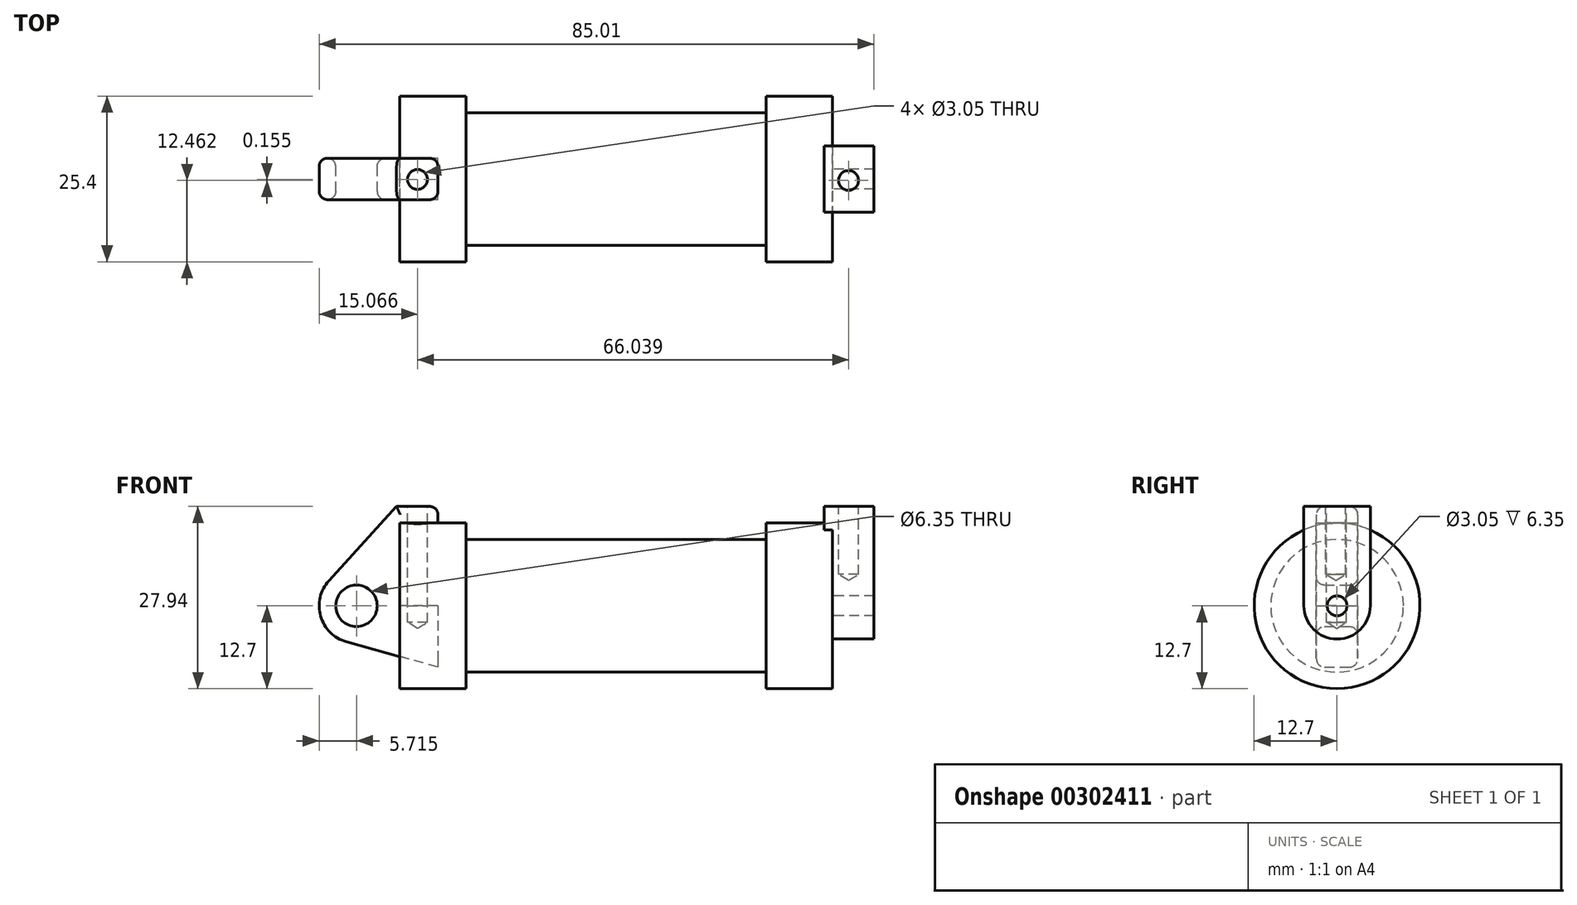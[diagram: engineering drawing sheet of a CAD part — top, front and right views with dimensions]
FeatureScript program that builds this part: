
annotation { "Feature Type Name" : "Feature", "Feature Type Description" : "" }
export const myFeature = defineFeature(function(context is Context, id is Id, definition is map)
    precondition{}
    {
        {
            var Q0;
            Q0=qCreatedBy(makeId("Front.planeOp"),FACE);
            var sketch = newSketch(context, id + "F0", { "sketchPlane" : qUnion([Q0])});
            skLineSegment(sketch, "E0", {"start": v(0, 0) * mm, "end": v(0, 12.7) * mm});
            skLineSegment(sketch, "E1", {"start": v(0, 12.7) * mm, "end": v(10.16, 12.7) * mm});
            skLineSegment(sketch, "E2", {"start": v(10.16, 12.7) * mm, "end": v(10.16, 10.16) * mm});
            skLineSegment(sketch, "E3", {"start": v(10.16, 10.16) * mm, "end": v(56.13, 10.16) * mm});
            skLineSegment(sketch, "E4", {"start": v(56.13, 10.16) * mm, "end": v(56.13, 12.7) * mm});
            skLineSegment(sketch, "E5", {"start": v(56.13, 12.7) * mm, "end": v(66.3, 12.7) * mm});
            skLineSegment(sketch, "E6", {"start": v(66.3, 12.7) * mm, "end": v(66.3, 0) * mm});
            skLineSegment(sketch, "E7", {"start": v(66.3, 0) * mm, "end": v(0, 0) * mm});
            skLineSegment(sketch, "E8", {"start": v(5.84, 15.24) * mm, "end": v(-0.5, 15.24) * mm});
            skLineSegment(sketch, "E9", {"start": v(-0.5, 15.24) * mm, "end": v(-10.88, 3.85) * mm});
            skLineSegment(sketch, "E10", {"start": v(0, 0) * mm, "end": v(-6.65, 0) * mm});
            skCircle(sketch, "E11", {"center": v(-6.65, 0) * mm, "radius": 5.72 * mm});
            skCircle(sketch, "E12", {"center": v(-6.65, 0) * mm, "radius": 3.18 * mm});
            skLineSegment(sketch, "E13", {"start": v(5.84, 15.24) * mm, "end": v(5.84, -9.4) * mm});
            skLineSegment(sketch, "E14", {"start": v(5.84, -9.4) * mm, "end": v(-8.18, -5.5) * mm});
            skSolve(sketch);
        }
        {
            var Q0;
            {var subQ1=sQuery(id+"F0.wireOp",EDGE,"E0");Q0=makeQuery(id+"F0.imprint","IMPRINT",FACE,{"disambiguationData":[TD([[makeQuery(id+"F0.imprint","IMPRINT",EDGE,{"derivedFrom":subQ1}),1.0]])]});}
            var Q1;
            {var subQ5=sQuery(id+"F0.wireOp",EDGE,"E12");Q1=makeQuery(id+"F0.imprint","IMPRINT",FACE,{"disambiguationData":[TD([[makeQuery(id+"F0.imprint","IMPRINT",EDGE,{"derivedFrom":subQ5}),-1.0]])]});}
            var Q2;
            {var subQ0=sQuery(id+"F0.wireOp",EDGE,"E14");Q2=makeQuery(id+"F0.imprint","IMPRINT",FACE,{"disambiguationData":[TD([[makeQuery(id+"F0.imprint","IMPRINT",EDGE,{"derivedFrom":subQ0}),-1.0]])]});}
            extrude(context, id + "F1", {"entities" : qUnion([Q0, Q1, Q2]), "endBound" : BoundingType.SYMMETRIC, "depth" : 6.35 * mm});
        }
        {
            var Q0;
            {var subQ0=sQuery(id+"F0.wireOp",EDGE,"E0");Q0=makeQuery(id+"F0.imprint","IMPRINT",FACE,{"disambiguationData":[TD([[makeQuery(id+"F0.imprint","IMPRINT",EDGE,{"derivedFrom":subQ0}),-1.0]])]});}
            var Q1;
            {var subQ0=sQuery(id+"F0.wireOp",EDGE,"E2");Q1=makeQuery(id+"F0.imprint","IMPRINT",FACE,{"disambiguationData":[TD([[makeQuery(id+"F0.imprint","IMPRINT",EDGE,{"derivedFrom":subQ0}),-1.0]])]});}
            var Q2;
            Q2=sQuery(id+"F0.wireOp",EDGE,"E7");
            revolve(context, id + "F2", {"entities" : qUnion([Q0, Q1]), "axis" : qUnion([Q2]), "revolveType" : RevolveType.FULL});
        }
        {
            var Q0;
            Q0=makeQuery(id+"F2.opRevolve","SWEPT_FACE",FACE,{"disambiguationData":[OSD([sQuery(id+"F0.wireOp",EDGE,"E6")])]});
            var sketch = newSketch(context, id + "F3", { "sketchPlane" : qUnion([Q0])});
            skCircle(sketch, "E15", {"center": v(0, 0) * mm, "radius": 1.52 * mm});
            skCircle(sketch, "E16", {"center": v(0, 0) * mm, "radius": 5.08 * mm});
            skLineSegment(sketch, "E17", {"start": v(-5.08, -0.01) * mm, "end": v(-5.08, 15.23) * mm});
            skLineSegment(sketch, "E18", {"start": v(5.08, -0.01) * mm, "end": v(5.08, 15.23) * mm});
            skLineSegment(sketch, "E19", {"start": v(-5.08, 15.23) * mm, "end": v(5.08, 15.23) * mm});
            skSolve(sketch);
        }
        {
            var Q0;
            {var subQ0=sQuery(id+"F3.wireOp",EDGE,"E19");Q0=makeQuery(id+"F3.imprint","IMPRINT",FACE,{"disambiguationData":[TD([[makeQuery(id+"F3.imprint","IMPRINT",EDGE,{"derivedFrom":subQ0}),-1.0]])]});}
            var Q1;
            Q1=makeQuery(id+"F3.imprint","IMPRINT",FACE,{"disambiguationData":[TD([[makeQuery(id+"F3.imprint","IMPRINT",EDGE,{"derivedFrom":sQuery(id+"F3.wireOp",EDGE,"E15")}),-1.0]])]});
            var Q2;
            {var subQ0=sQuery(id+"F3.wireOp",EDGE,"E17");var subQ1=sQuery(id+"F3.wireOp",EDGE,"E16");var subQ2=makeQuery(id+"F3.imprint","INTERSECT",VERTEX,{"derivedFrom":[subQ1,subQ0]});Q2=makeQuery(id+"F3.imprint","IMPRINT",FACE,{"disambiguationData":[TD([[makeQuery(id+"F3.imprint","IMPRINT",EDGE,{"disambiguationData":[TD([[subQ2,1.0]])],"derivedFrom":subQ1}),-1.0]])]});}
            extrude(context, id + "F4", {"entities" : qUnion([Q0, Q1, Q2]), "operationType" : NewBodyOperationType.ADD, "depth" : 6.35 * mm, "hasSecondDirection" : true, "secondDirectionOppositeDirection" : true, "secondDirectionDepth" : 1.27 * mm});
        }
        {
            var Q0;
            Q0=makeQuery(id+"F1.opExtrude","SWEPT_FACE",FACE,{"disambiguationData":[OSD([sQuery(id+"F0.wireOp",EDGE,"E8")])]});
            var sketch = newSketch(context, id + "F5", { "sketchPlane" : qUnion([Q0])});
            skCircle(sketch, "E20", {"center": v(2.7, -0.08) * mm, "radius": 1.52 * mm});
            skCircle(sketch, "E21", {"center": v(69.07, -0.25) * mm, "radius": 1.52 * mm});
            skSolve(sketch);
        }
        {
            var Q0;
            Q0=sQuery(id+"F5.wireOp",VERTEX,"E20.center");
            var Q1;
            Q1=makeQuery(id+"F2.opRevolve","SWEPT_BODY",BODY,{"disambiguationData":[OSD([sQuery(id+"F0.wireOp",EDGE,"E0"),sQuery(id+"F0.wireOp",EDGE,"E1"),sQuery(id+"F0.wireOp",EDGE,"E2"),sQuery(id+"F0.wireOp",EDGE,"E3"),sQuery(id+"F0.wireOp",EDGE,"E4"),sQuery(id+"F0.wireOp",EDGE,"E5"),sQuery(id+"F0.wireOp",EDGE,"E6"),sQuery(id+"F0.wireOp",EDGE,"E7")])]});
            var Q2;
            Q2=makeQuery(id+"F1.opExtrude","SWEPT_BODY",BODY,{"disambiguationData":[OSD([sQuery(id+"F0.wireOp",EDGE,"E0"),sQuery(id+"F0.wireOp",EDGE,"E1"),sQuery(id+"F0.wireOp",EDGE,"E7"),sQuery(id+"F0.wireOp",EDGE,"E8"),sQuery(id+"F0.wireOp",EDGE,"E9"),sQuery(id+"F0.wireOp",EDGE,"E11"),sQuery(id+"F0.wireOp",EDGE,"E12"),sQuery(id+"F0.wireOp",EDGE,"E13"),sQuery(id+"F0.wireOp",EDGE,"E14")])]});
            hole(context, id + "F6", {"style" : HoleStyle.SIMPLE, "endStyle" : HoleEndStyle.BLIND, "holeDiameter" : 3.05 * mm, "holeDepth" : 17.78 * mm, "tappedDepth" : 12.7 * mm, "tapClearance" : 3, "locations" : qUnion([Q0]), "scope" : qUnion([Q1, Q2])});
        }
        {
            var Q0;
            Q0=makeQuery(id+"F4.opExtrude","SWEPT_FACE",FACE,{"disambiguationData":[OSD([sQuery(id+"F3.wireOp",EDGE,"E19")])]});
            var sketch = newSketch(context, id + "F7", { "sketchPlane" : qUnion([Q0])});
            skCircle(sketch, "E22", {"center": v(68.74, -0.24) * mm, "radius": 1.56 * mm});
            skSolve(sketch);
        }
        {
            var Q0;
            Q0=sQuery(id+"F7.wireOp",VERTEX,"E22.center");
            var Q1;
            Q1=makeQuery(id+"F2.opRevolve","SWEPT_BODY",BODY,{"disambiguationData":[OSD([sQuery(id+"F0.wireOp",EDGE,"E0"),sQuery(id+"F0.wireOp",EDGE,"E1"),sQuery(id+"F0.wireOp",EDGE,"E2"),sQuery(id+"F0.wireOp",EDGE,"E3"),sQuery(id+"F0.wireOp",EDGE,"E4"),sQuery(id+"F0.wireOp",EDGE,"E5"),sQuery(id+"F0.wireOp",EDGE,"E6"),sQuery(id+"F0.wireOp",EDGE,"E7")])]});
            hole(context, id + "F8", {"style" : HoleStyle.SIMPLE, "endStyle" : HoleEndStyle.BLIND, "holeDiameter" : 3.05 * mm, "holeDepth" : 10.4 * mm, "tappedDepth" : 12.7 * mm, "tapClearance" : 3, "locations" : qUnion([Q0]), "scope" : qUnion([Q1])});
        }
        {
            var Q0;
            Q0=makeQuery(id+"F2.opRevolve","SWEPT_EDGE",EDGE,{"disambiguationData":[OSD([sQuery(id+"F0.wireOp",EDGE,"E1"),sQuery(id+"F0.wireOp",EDGE,"E2")])]});
            var Q1;
            Q1=makeQuery(id+"F2.opRevolve","SWEPT_FACE",FACE,{"disambiguationData":[OSD([sQuery(id+"F0.wireOp",EDGE,"E1")])]});
            var Q2;
            Q2=makeQuery(id+"F1.opExtrude","CAP_EDGE",EDGE,{"disambiguationData":[OSD([sQuery(id+"F0.wireOp",EDGE,"E9")])],"isStart":true});
            var Q3;
            Q3=makeQuery(id+"F1.opExtrude","CAP_EDGE",EDGE,{"disambiguationData":[OSD([sQuery(id+"F0.wireOp",EDGE,"E12")])],"isStart":true});
            var Q4;
            Q4=makeQuery(id+"F1.opExtrude","CAP_EDGE",EDGE,{"disambiguationData":[OSD([sQuery(id+"F0.wireOp",EDGE,"E8")])],"isStart":true});
            var Q5;
            {var subQ0=sQuery(id+"F0.wireOp",EDGE,"E13");Q5=makeQuery(id+"F1.opExtrude","CAP_EDGE",EDGE,{"disambiguationData":[OSD([subQ0]),TDD([makeQuery(id+"F0.imprint","IMPRINT",EDGE,{"disambiguationData":[TD([[makeQuery(id+"F0.imprint","INTERSECT",VERTEX,{"derivedFrom":[sQuery(id+"F0.wireOp",EDGE,"E8"),subQ0]}),-1.0]])],"derivedFrom":subQ0})])],"isStart":true});}
            var Q6;
            Q6=makeQuery(id+"F2.opRevolve","SWEPT_EDGE",EDGE,{"disambiguationData":[OSD([sQuery(id+"F0.wireOp",EDGE,"E4"),sQuery(id+"F0.wireOp",EDGE,"E5")])]});
            var Q7;
            Q7=makeQuery(id+"F2.opRevolve","SWEPT_EDGE",EDGE,{"disambiguationData":[OSD([sQuery(id+"F0.wireOp",EDGE,"E5"),sQuery(id+"F0.wireOp",EDGE,"E6")])]});
            var Q8;
            Q8=makeQuery(id+"F1.opExtrude","CAP_EDGE",EDGE,{"disambiguationData":[OSD([sQuery(id+"F0.wireOp",EDGE,"E9")])],"isStart":false});
            var Q9;
            Q9=makeQuery(id+"F1.opExtrude","CAP_EDGE",EDGE,{"disambiguationData":[OSD([sQuery(id+"F0.wireOp",EDGE,"E12")])],"isStart":false});
            var Q10;
            Q10=makeQuery(id+"F1.opExtrude","CAP_EDGE",EDGE,{"disambiguationData":[OSD([sQuery(id+"F0.wireOp",EDGE,"E8")])],"isStart":false});
            var Q11;
            Q11=makeQuery(id+"F6.hole-0.boolean.opBoolean","COPY",EDGE,{"derivedFrom":makeQuery(id+"F6.hole-0.opRevolve","SWEPT_EDGE",EDGE,{"disambiguationData":[OSD([sQuery(id+"F6.hole-0.sketch.wireOp",EDGE,"core_line_2"),sQuery(id+"F6.hole-0.sketch.wireOp",EDGE,"core_line_3")])]})});
            var Q12;
            Q12=makeQuery(id+"F1.opExtrude","SWEPT_EDGE",EDGE,{"disambiguationData":[OSD([sQuery(id+"F0.wireOp",EDGE,"E8"),sQuery(id+"F0.wireOp",EDGE,"E13")])]});
            var Q13;
            Q13=makeQuery(id+"F4.opExtrude","SWEPT_FACE",FACE,{"disambiguationData":[OSD([sQuery(id+"F3.wireOp",EDGE,"E19")])]});
            var Q14;
            Q14=makeQuery(id+"F4.opExtrude","CAP_EDGE",EDGE,{"disambiguationData":[OSD([sQuery(id+"F3.wireOp",EDGE,"E17")])],"isStart":false});
            var Q15;
            {var subQ0=sQuery(id+"F0.wireOp",EDGE,"E13");Q15=makeQuery(id+"F1.opExtrude","CAP_EDGE",EDGE,{"disambiguationData":[OSD([subQ0]),TDD([makeQuery(id+"F0.imprint","IMPRINT",EDGE,{"disambiguationData":[TD([[makeQuery(id+"F0.imprint","INTERSECT",VERTEX,{"derivedFrom":[sQuery(id+"F0.wireOp",EDGE,"E8"),subQ0]}),-1.0]])],"derivedFrom":subQ0})])],"isStart":false});}
            var Q16;
            Q16=makeQuery(id+"F4.opExtrude","SWEPT_FACE",FACE,{"disambiguationData":[OSD([sQuery(id+"F3.wireOp",EDGE,"E16")])]});
            var Q17;
            Q17=makeQuery(id+"F4.opExtrude","CAP_EDGE",EDGE,{"disambiguationData":[OSD([sQuery(id+"F3.wireOp",EDGE,"E15")])],"isStart":false});
            fillet(context, id + "F9", {"entities" : qUnion([Q0, Q1, Q2, Q3, Q4, Q5, Q6, Q7, Q8, Q9, Q10, Q11, Q12, Q13, Q14, Q15, Q16, Q17]), "radius" : 1.27 * mm, "tangentPropagation" : true, "allowEdgeOverflow" : false});
        }
    });
